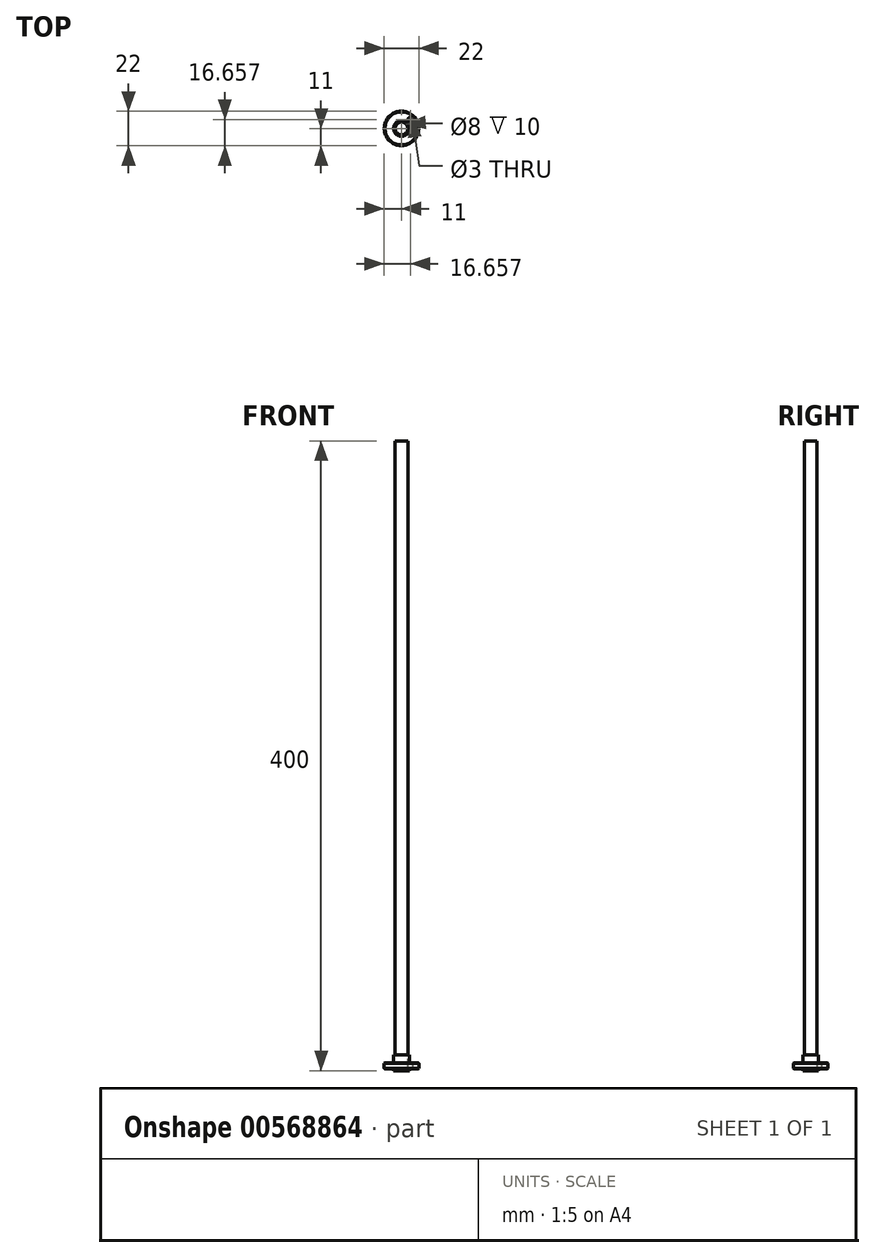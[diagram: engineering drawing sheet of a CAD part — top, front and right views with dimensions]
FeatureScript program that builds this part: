
annotation { "Feature Type Name" : "Feature", "Feature Type Description" : "" }
export const myFeature = defineFeature(function(context is Context, id is Id, definition is map)
    precondition{}
    {
        {
            var Q0;
            Q0=qCreatedBy(makeId("Top.planeOp"),FACE);
            var sketch = newSketch(context, id + "F0", { "sketchPlane" : qUnion([Q0])});
            skCircle(sketch, "E0", {"center": v(0, 0) * mm, "radius": 4 * mm});
            skSolve(sketch);
        }
        {
            var Q0;
            Q0 = qSketchRegion(id + "F0", true);
            extrude(context, id + "F1", {"entities" : qUnion([Q0]), "depth" : 400 * mm, "offsetDistance" : 25 * mm});
        }
        {
            var Q0;
            Q0=qCreatedBy(makeId("Front.planeOp"),FACE);
            var sketch = newSketch(context, id + "F2", { "sketchPlane" : qUnion([Q0])});
            skLineSegment(sketch, "E1", {"start": v(0, 28.63) * mm, "end": v(0, -11.53) * mm, "construction": true});
            skLineSegment(sketch, "E2", {"start": v(-4, 0) * mm, "end": v(-4, 10) * mm});
            skLineSegment(sketch, "E3", {"start": v(-4, 10) * mm, "end": v(-5, 10) * mm});
            skLineSegment(sketch, "E4", {"start": v(-5, 10) * mm, "end": v(-5, 5) * mm});
            skLineSegment(sketch, "E5", {"start": v(-5, 5) * mm, "end": v(-11, 5) * mm});
            skLineSegment(sketch, "E6", {"start": v(-11, 5) * mm, "end": v(-11, 1) * mm});
            skLineSegment(sketch, "E7", {"start": v(-11, 1) * mm, "end": v(-5, 1) * mm});
            skLineSegment(sketch, "E8", {"start": v(-5, 1) * mm, "end": v(-5, 0) * mm});
            skLineSegment(sketch, "E9", {"start": v(-5, 0) * mm, "end": v(-4, 0) * mm});
            skSolve(sketch);
        }
        {
            var Q0;
            Q0 = qSketchRegion(id + "F2", true);
            var Q1;
            Q1=sQuery(id+"F2.wireOp",EDGE,"E1");
            revolve(context, id + "F3", {"entities" : qUnion([Q0]), "axis" : qUnion([Q1]), "revolveType" : RevolveType.FULL});
        }
        {
            var Q0;
            Q0=makeQuery(id+"F3.opRevolve","SWEPT_EDGE",EDGE,{"disambiguationData":[OSD([sQuery(id+"F2.wireOp",EDGE,"E5"),sQuery(id+"F2.wireOp",EDGE,"E6")])]});
            var Q1;
            Q1=makeQuery(id+"F3.opRevolve","SWEPT_EDGE",EDGE,{"disambiguationData":[OSD([sQuery(id+"F2.wireOp",EDGE,"E6"),sQuery(id+"F2.wireOp",EDGE,"E7")])]});
            chamfer(context, id + "F4", {"entities" : qUnion([Q0, Q1]), "width" : .5 * mm, "tangentPropagation" : true});
        }
        {
            var Q0;
            Q0=makeQuery(id+"F3.opRevolve","SWEPT_FACE",FACE,{"disambiguationData":[OSD([sQuery(id+"F2.wireOp",EDGE,"E5")])]});
            var sketch = newSketch(context, id + "F5", { "sketchPlane" : qUnion([Q0])});
            skCircle(sketch, "E10", {"center": v(5.66, 5.66) * mm, "radius": 1.5 * mm});
            skLineSegment(sketch, "E11", {"start": v(0, 0) * mm, "end": v(5.66, 5.66) * mm, "construction": true});
            skLineSegment(sketch, "E12", {"start": v(0, 0) * mm, "end": v(14.12, 0) * mm, "construction": true});
            skSolve(sketch);
        }
        {
            var Q0;
            Q0 = qSketchRegion(id + "F5", true);
            extrude(context, id + "F6", {"entities" : qUnion([Q0]), "operationType" : NewBodyOperationType.REMOVE, "oppositeDirection" : true, "depth" : 25 * mm, "offsetDistance" : 25 * mm});
        }
    });
